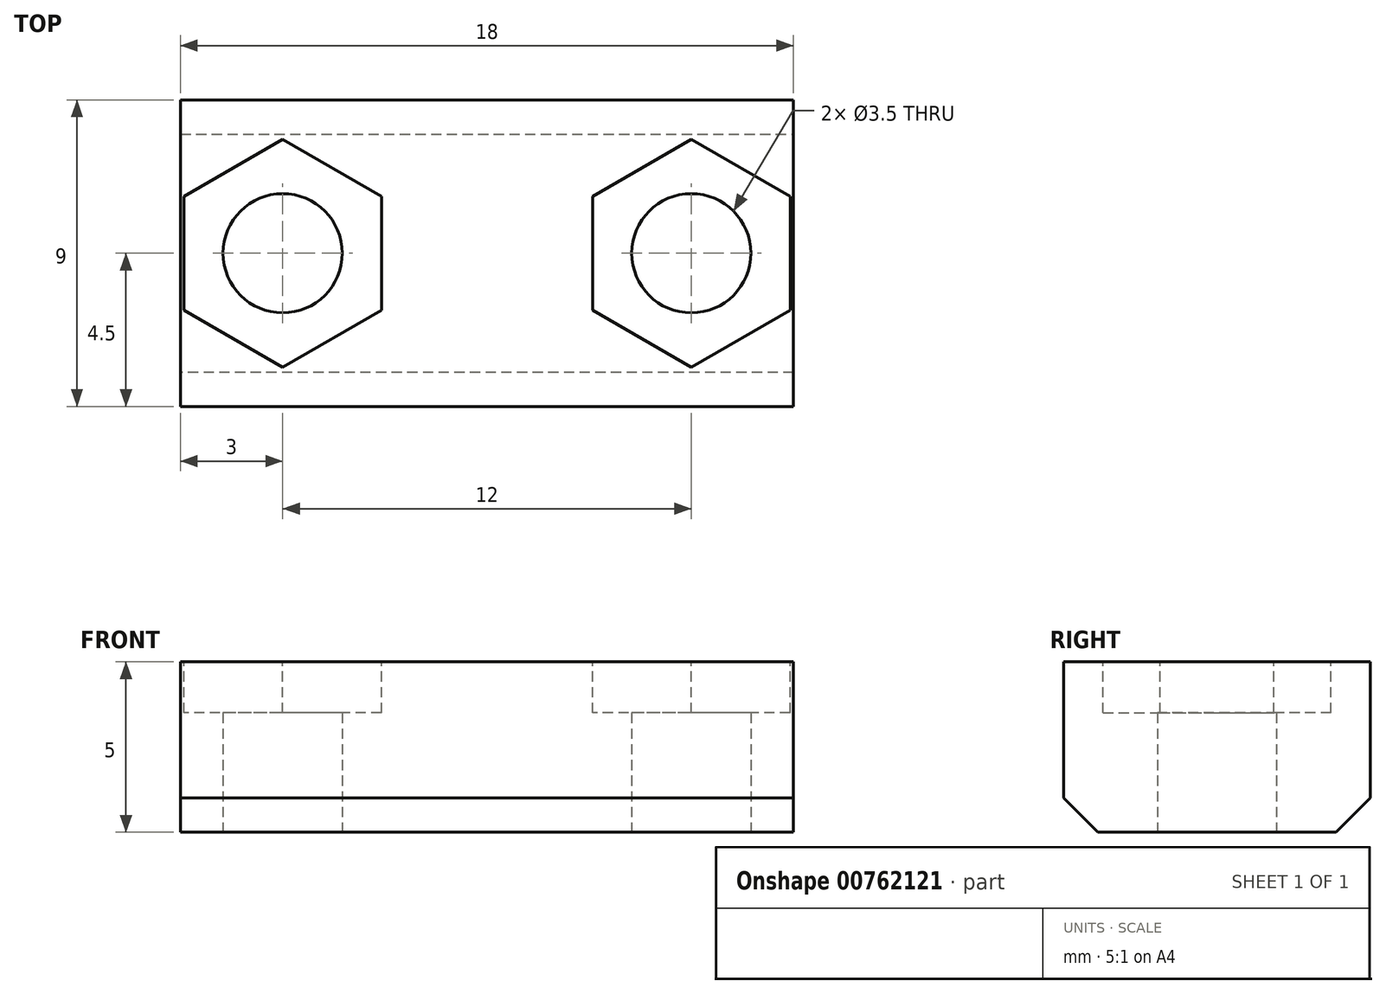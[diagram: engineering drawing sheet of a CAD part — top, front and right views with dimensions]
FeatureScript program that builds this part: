
annotation { "Feature Type Name" : "Feature", "Feature Type Description" : "" }
export const myFeature = defineFeature(function(context is Context, id is Id, definition is map)
    precondition{}
    {
        {
            var Q0;
            Q0=qCreatedBy(makeId("Top.planeOp"),FACE);
            var sketch = newSketch(context, id + "F0", { "sketchPlane" : qUnion([Q0])});
            skLineSegment(sketch, "E0.bottom", {"start": v(-9, -4.5) * mm, "end": v(9, -4.5) * mm});
            skLineSegment(sketch, "E0.top", {"start": v(-9, 4.5) * mm, "end": v(9, 4.5) * mm});
            skLineSegment(sketch, "E0.left", {"start": v(-9, -4.5) * mm, "end": v(-9, 4.5) * mm});
            skLineSegment(sketch, "E0.right", {"start": v(9, -4.5) * mm, "end": v(9, 4.5) * mm});
            skCircle(sketch, "E1", {"center": v(-6, 0) * mm, "radius": 1.75 * mm});
            skCircle(sketch, "E2", {"center": v(6, 0) * mm, "radius": 1.75 * mm});
            skPoint(sketch, "E3", {"position": v(-9, 0) * mm});
            skPoint(sketch, "E4", {"position": v(0, -4.5) * mm});
            skLineSegment(sketch, "E5", {"start": v(-6, 0) * mm, "end": v(6, 0) * mm, "construction": true});
            skPoint(sketch, "E6", {"position": v(0, 0) * mm});
            skSolve(sketch);
        }
        {
            var Q0;
            Q0=makeQuery(id+"F0.imprint","IMPRINT",FACE,{"disambiguationData":[TD([[makeQuery(id+"F0.imprint","IMPRINT",EDGE,{"derivedFrom":sQuery(id+"F0.wireOp",EDGE,"E0.bottom")}),1.0]])]});
            extrude(context, id + "F1", {"entities" : qUnion([Q0]), "depth" : 5 * mm, "offsetDistance" : 25 * mm});
        }
        {
            var Q0;
            Q0=makeQuery(id+"F1.opExtrude","CAP_FACE",FACE,{"disambiguationData":[OSD([sQuery(id+"F0.wireOp",EDGE,"E0.bottom"),sQuery(id+"F0.wireOp",EDGE,"E0.top"),sQuery(id+"F0.wireOp",EDGE,"E0.left"),sQuery(id+"F0.wireOp",EDGE,"E0.right"),sQuery(id+"F0.wireOp",EDGE,"E1"),sQuery(id+"F0.wireOp",EDGE,"E2")])],"isStart":false});
            var sketch = newSketch(context, id + "F2", { "sketchPlane" : qUnion([Q0])});
            skCircle(sketch, "E7.0", {"center": v(-6, 0) * mm, "radius": 1.75 * mm});
            skCircle(sketch, "E8.0", {"center": v(6, 0) * mm, "radius": 1.75 * mm});
            skCircle(sketch, "E9.cCircle", {"center": v(-6, 0) * mm, "radius": 2.9 * mm, "construction": true});
            skLineSegment(sketch, "E9.0", {"start": v(-8.9, -1.67) * mm, "end": v(-8.9, 1.67) * mm});
            skLineSegment(sketch, "E9.1", {"start": v(-8.9, 1.67) * mm, "end": v(-6, 3.35) * mm});
            skLineSegment(sketch, "E9.2", {"start": v(-6, 3.35) * mm, "end": v(-3.1, 1.67) * mm});
            skLineSegment(sketch, "E9.3", {"start": v(-3.1, 1.67) * mm, "end": v(-3.1, -1.67) * mm});
            skLineSegment(sketch, "E9.4", {"start": v(-3.1, -1.67) * mm, "end": v(-6, -3.35) * mm});
            skLineSegment(sketch, "E9.5", {"start": v(-6, -3.35) * mm, "end": v(-8.9, -1.67) * mm});
            skPoint(sketch, "E9.0.midPoint", {"position": v(-8.9, 0) * mm});
            skCircle(sketch, "E10.cCircle", {"center": v(6, 0) * mm, "radius": 2.9 * mm, "construction": true});
            skLineSegment(sketch, "E10.0", {"start": v(3.1, -1.67) * mm, "end": v(3.1, 1.67) * mm});
            skLineSegment(sketch, "E10.1", {"start": v(3.1, 1.67) * mm, "end": v(6, 3.35) * mm});
            skLineSegment(sketch, "E10.2", {"start": v(6, 3.35) * mm, "end": v(8.9, 1.67) * mm});
            skLineSegment(sketch, "E10.3", {"start": v(8.9, 1.67) * mm, "end": v(8.9, -1.67) * mm});
            skLineSegment(sketch, "E10.4", {"start": v(8.9, -1.67) * mm, "end": v(6, -3.35) * mm});
            skLineSegment(sketch, "E10.5", {"start": v(6, -3.35) * mm, "end": v(3.1, -1.67) * mm});
            skPoint(sketch, "E10.0.midPoint", {"position": v(3.1, 0) * mm});
            skSolve(sketch);
        }
        {
            var Q0;
            Q0=makeQuery(id+"F2.imprint","IMPRINT",FACE,{"disambiguationData":[TD([[makeQuery(id+"F2.imprint","IMPRINT",EDGE,{"derivedFrom":sQuery(id+"F2.wireOp",EDGE,"E7.0")}),-1.0]])]});
            var Q1;
            Q1=makeQuery(id+"F2.imprint","IMPRINT",FACE,{"disambiguationData":[TD([[makeQuery(id+"F2.imprint","IMPRINT",EDGE,{"derivedFrom":sQuery(id+"F2.wireOp",EDGE,"E8.0")}),-1.0]])]});
            extrude(context, id + "F3", {"entities" : qUnion([Q0, Q1]), "operationType" : NewBodyOperationType.REMOVE, "oppositeDirection" : true, "depth" : 1.5 * mm, "offsetDistance" : 25 * mm});
        }
        {
            var Q0;
            Q0=makeQuery(id+"F1.opExtrude","CAP_EDGE",EDGE,{"disambiguationData":[OSD([sQuery(id+"F0.wireOp",EDGE,"E0.bottom")])],"isStart":true});
            var Q1;
            Q1=makeQuery(id+"F1.opExtrude","CAP_EDGE",EDGE,{"disambiguationData":[OSD([sQuery(id+"F0.wireOp",EDGE,"E0.top")])],"isStart":true});
            chamfer(context, id + "F4", {"entities" : qUnion([Q0, Q1]), "width" : 1 * mm, "tangentPropagation" : true});
        }
    });
